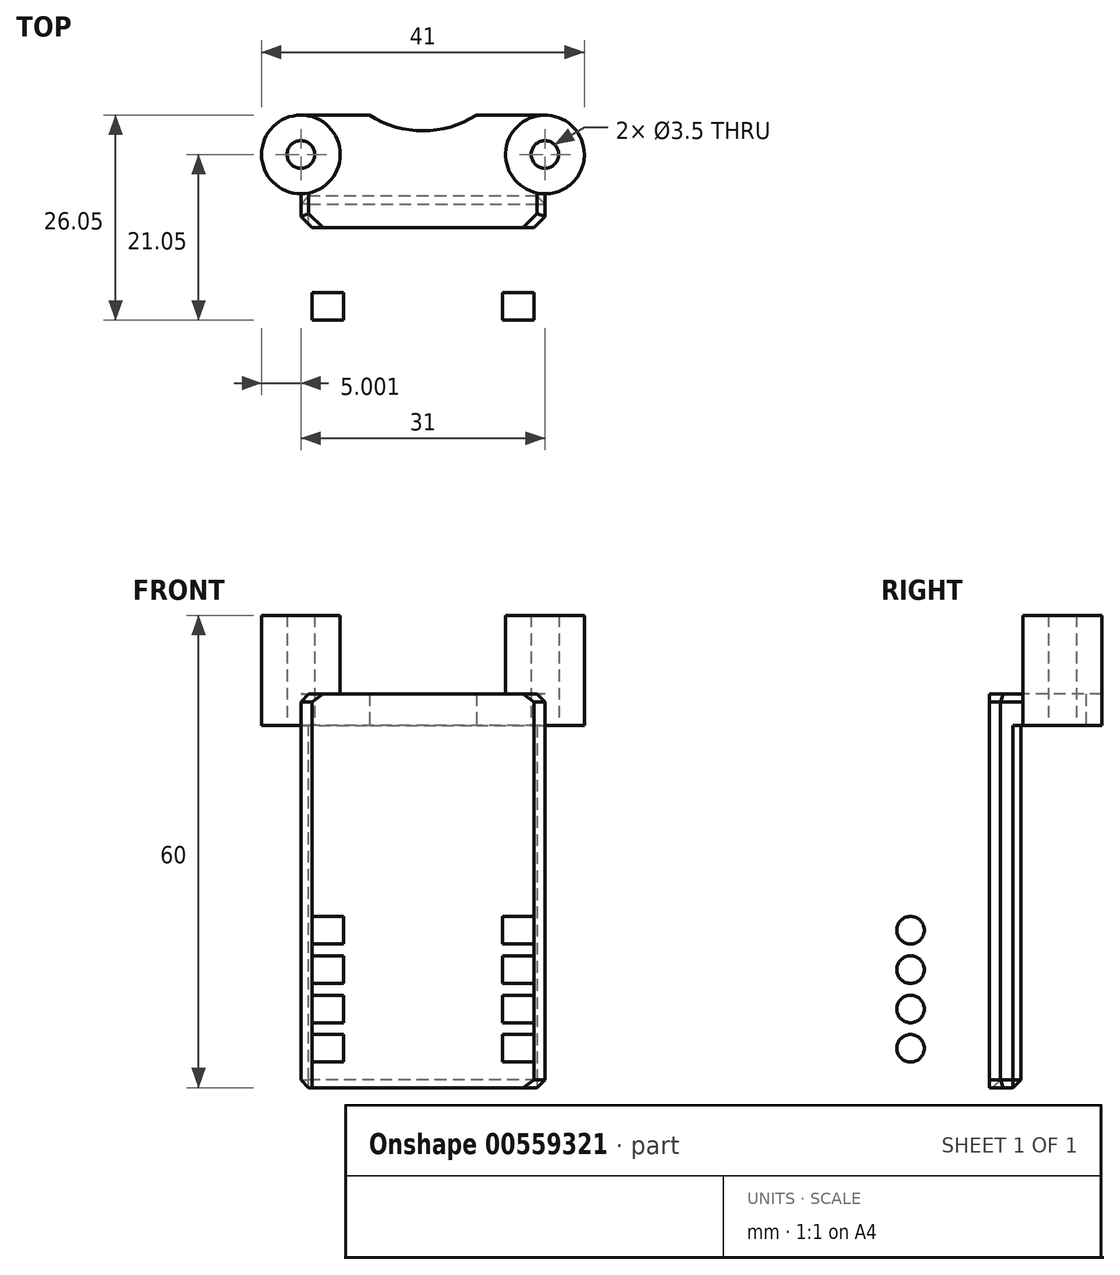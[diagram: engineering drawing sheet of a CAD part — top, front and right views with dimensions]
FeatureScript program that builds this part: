
annotation { "Feature Type Name" : "Feature", "Feature Type Description" : "" }
export const myFeature = defineFeature(function(context is Context, id is Id, definition is map)
    precondition{}
    {
        {
            var Q0;
            Q0=qCreatedBy(makeId("Top.planeOp"),FACE);
            var sketch = newSketch(context, id + "F0", { "sketchPlane" : qUnion([Q0])});
            skLineSegment(sketch, "E0", {"start": v(-4.15, -31) * mm, "end": v(26.85, -31) * mm});
            skCircle(sketch, "E1", {"center": v(26.85, -31) * mm, "radius": 1.75 * mm});
            skCircle(sketch, "E2", {"center": v(-4.15, -31) * mm, "radius": 1.75 * mm});
            skCircle(sketch, "E3", {"center": v(-4.15, -31) * mm, "radius": 5 * mm});
            skCircle(sketch, "E4", {"center": v(26.85, -31) * mm, "radius": 5 * mm});
            skLineSegment(sketch, "E5", {"start": v(-4.15, -31) * mm, "end": v(-4.15, -26) * mm, "construction": true});
            skLineSegment(sketch, "E6", {"start": v(-4.15, -26) * mm, "end": v(26.85, -26) * mm});
            skLineSegment(sketch, "E7", {"start": v(26.85, -26) * mm, "end": v(26.85, -36) * mm, "construction": true});
            skLineSegment(sketch, "E8", {"start": v(26.85, -36) * mm, "end": v(-4.15, -36) * mm});
            skLineSegment(sketch, "E9", {"start": v(-4.15, -36) * mm, "end": v(-4.15, -31) * mm, "construction": true});
            skLineSegment(sketch, "E10", {"start": v(26.85, -31) * mm, "end": v(26.85, 0) * mm});
            skLineSegment(sketch, "E11", {"start": v(26.85, 0) * mm, "end": v(-4.15, 0) * mm});
            skLineSegment(sketch, "E12", {"start": v(-4.15, 0) * mm, "end": v(-4.15, -31) * mm});
            skLineSegment(sketch, "E13", {"start": v(-4.15, -31) * mm, "end": v(26.85, 0) * mm, "construction": true});
            skLineSegment(sketch, "E14", {"start": v(-4.15, 0) * mm, "end": v(26.85, -31) * mm, "construction": true});
            skCircle(sketch, "E15", {"center": v(11.35, -15.5) * mm, "radius": 12.5 * mm});
            skSolve(sketch);
        }
        {
            var Q0;
            Q0=makeQuery(id+"F0.imprint","IMPRINT",FACE,{"disambiguationData":[TD([[makeQuery(id+"F0.imprint","IMPRINT",EDGE,{"derivedFrom":sQuery(id+"F0.wireOp",EDGE,"E2")}),-1.0]])]});
            var Q1;
            {var subQ5=sQuery(id+"F0.wireOp",EDGE,"E6");Q1=makeQuery(id+"F0.imprint","IMPRINT",FACE,{"disambiguationData":[TD([[makeQuery(id+"F0.imprint","IMPRINT",EDGE,{"derivedFrom":subQ5}),-1.0]])]});}
            var Q2;
            Q2=makeQuery(id+"F0.imprint","IMPRINT",FACE,{"disambiguationData":[TD([[makeQuery(id+"F0.imprint","IMPRINT",EDGE,{"derivedFrom":sQuery(id+"F0.wireOp",EDGE,"E1")}),-1.0]])]});
            var Q3;
            {var subQ5=sQuery(id+"F0.wireOp",EDGE,"E8");Q3=makeQuery(id+"F0.imprint","IMPRINT",FACE,{"disambiguationData":[TD([[makeQuery(id+"F0.imprint","IMPRINT",EDGE,{"derivedFrom":subQ5}),-1.0]])]});}
            var Q4;
            {var subQ1=sQuery(id+"F0.wireOp",EDGE,"E4");var subQ4=sQuery(id+"F0.wireOp",EDGE,"E0");var subQ5=makeQuery(id+"F0.imprint","INTERSECT",VERTEX,{"derivedFrom":[subQ4,subQ1]});Q4=makeQuery(id+"F0.imprint","IMPRINT",FACE,{"disambiguationData":[TD([[makeQuery(id+"F0.imprint","IMPRINT",EDGE,{"disambiguationData":[TD([[subQ5,-1.0]])],"derivedFrom":subQ4}),-1.0]])]});}
            var Q5;
            {var subQ4=sQuery(id+"F0.wireOp",EDGE,"E2");var subQ5=sQuery(id+"F0.wireOp",EDGE,"E0");var subQ6=makeQuery(id+"F0.imprint","INTERSECT",VERTEX,{"derivedFrom":[subQ5,subQ4]});Q5=makeQuery(id+"F0.imprint","IMPRINT",FACE,{"disambiguationData":[TD([[makeQuery(id+"F0.imprint","IMPRINT",EDGE,{"disambiguationData":[TD([[subQ6,-1.0]])],"derivedFrom":subQ5}),-1.0]])]});}
            extrude(context, id + "F1", {"entities" : qUnion([Q0, Q1, Q2, Q3, Q4, Q5]), "depth" : 4 * mm, "offsetDistance" : 25 * mm});
        }
        {
            var Q0;
            Q0=makeQuery(id+"F0.imprint","IMPRINT",FACE,{"disambiguationData":[TD([[makeQuery(id+"F0.imprint","IMPRINT",EDGE,{"derivedFrom":sQuery(id+"F0.wireOp",EDGE,"E2")}),-1.0]])]});
            var Q1;
            Q1=makeQuery(id+"F0.imprint","IMPRINT",FACE,{"disambiguationData":[TD([[makeQuery(id+"F0.imprint","IMPRINT",EDGE,{"derivedFrom":sQuery(id+"F0.wireOp",EDGE,"E1")}),-1.0]])]});
            var Q2;
            {var subQ4=sQuery(id+"F0.wireOp",EDGE,"E2");var subQ5=sQuery(id+"F0.wireOp",EDGE,"E0");var subQ6=makeQuery(id+"F0.imprint","INTERSECT",VERTEX,{"derivedFrom":[subQ5,subQ4]});Q2=makeQuery(id+"F0.imprint","IMPRINT",FACE,{"disambiguationData":[TD([[makeQuery(id+"F0.imprint","IMPRINT",EDGE,{"disambiguationData":[TD([[subQ6,-1.0]])],"derivedFrom":subQ5}),-1.0]])]});}
            var Q3;
            {var subQ1=sQuery(id+"F0.wireOp",EDGE,"E4");var subQ4=sQuery(id+"F0.wireOp",EDGE,"E0");var subQ5=makeQuery(id+"F0.imprint","INTERSECT",VERTEX,{"derivedFrom":[subQ4,subQ1]});Q3=makeQuery(id+"F0.imprint","IMPRINT",FACE,{"disambiguationData":[TD([[makeQuery(id+"F0.imprint","IMPRINT",EDGE,{"disambiguationData":[TD([[subQ5,-1.0]])],"derivedFrom":subQ4}),-1.0]])]});}
            extrude(context, id + "F2", {"entities" : qUnion([Q0, Q1, Q2, Q3]), "operationType" : NewBodyOperationType.ADD, "depth" : 14 * mm, "offsetDistance" : 25 * mm});
        }
        {
            var Q0;
            Q0=makeQuery(id+"F1.opExtrude","SWEPT_FACE",FACE,{"disambiguationData":[OSD([sQuery(id+"F0.wireOp",EDGE,"E8")])]});
            extrude(context, id + "F3", {"entities" : qUnion([Q0]), "operationType" : NewBodyOperationType.ADD, "depth" : 4.3 * mm, "offsetDistance" : 25 * mm});
        }
        {
            var Q0;
            {var subQ0=sQuery(id+"F0.wireOp",EDGE,"E8");Q0=makeQuery(id+"F3.boolean.opBoolean","MERGE",FACE,{"derivedFrom":[makeQuery(id+"F1.opExtrude","CAP_FACE",FACE,{"disambiguationData":[OSD([sQuery(id+"F0.wireOp",EDGE,"E1"),sQuery(id+"F0.wireOp",EDGE,"E2"),sQuery(id+"F0.wireOp",EDGE,"E3"),sQuery(id+"F0.wireOp",EDGE,"E4"),sQuery(id+"F0.wireOp",EDGE,"E6"),subQ0,sQuery(id+"F0.wireOp",EDGE,"E15")])],"isStart":true}),makeQuery(id+"F3.opExtrude","SWEPT_FACE",FACE,{"disambiguationData":[OSD([subQ0]),TDD([makeQuery(id+"F1.opExtrude","CAP_EDGE",EDGE,{"disambiguationData":[OSD([subQ0])],"isStart":true})])]})]});}
            var sketch = newSketch(context, id + "F4", { "sketchPlane" : qUnion([Q0])});
            skLineSegment(sketch, "E16.bottom", {"start": v(26.85, 40.3) * mm, "end": v(-4.15, 40.3) * mm});
            skLineSegment(sketch, "E16.top", {"start": v(26.85, 36.3) * mm, "end": v(-4.15, 36.3) * mm});
            skLineSegment(sketch, "E16.left", {"start": v(26.85, 40.3) * mm, "end": v(26.85, 36.3) * mm});
            skLineSegment(sketch, "E16.right", {"start": v(-4.15, 40.3) * mm, "end": v(-4.15, 36.3) * mm});
            skSolve(sketch);
        }
        {
            var Q0;
            Q0=makeQuery(id+"F4.imprint","IMPRINT",FACE,{"disambiguationData":[TD([[makeQuery(id+"F4.imprint","IMPRINT",EDGE,{"derivedFrom":sQuery(id+"F4.wireOp",EDGE,"E16.bottom")}),1.0]])]});
            extrude(context, id + "F5", {"entities" : qUnion([Q0]), "operationType" : NewBodyOperationType.ADD, "depth" : 46 * mm, "offsetDistance" : 25 * mm});
        }
        {
            var Q0;
            Q0=makeQuery(id+"F5.boolean.opBoolean","MERGE",FACE,{"derivedFrom":[makeQuery(id+"F3.opExtrude","CAP_FACE",FACE,{"disambiguationData":[OSD([sQuery(id+"F0.wireOp",EDGE,"E8")])],"isStart":false}),makeQuery(id+"F5.opExtrude","SWEPT_FACE",FACE,{"disambiguationData":[OSD([sQuery(id+"F4.wireOp",EDGE,"E16.bottom")])]})]});
            var sketch = newSketch(context, id + "F6", { "sketchPlane" : qUnion([Q0])});
            skLineSegment(sketch, "E17", {"start": v(11.35, 4) * mm, "end": v(11.35, -46) * mm, "construction": true});
            skLineSegment(sketch, "E18", {"start": v(21.45, -21) * mm, "end": v(1.25, -21) * mm, "construction": true});
            skPoint(sketch, "E18.startSnap0", {"position": v(11.35, -21) * mm});
            skLineSegment(sketch, "E19", {"start": v(21.45, -46) * mm, "end": v(21.45, 4) * mm});
            skLineSegment(sketch, "E20", {"start": v(1.25, 4) * mm, "end": v(1.25, -46) * mm});
            skLineSegment(sketch, "E21", {"start": v(21.45, -21) * mm, "end": v(25.45, -21) * mm, "construction": true});
            skLineSegment(sketch, "E22", {"start": v(1.25, -21) * mm, "end": v(-2.75, -21) * mm, "construction": true});
            skLineSegment(sketch, "E23", {"start": v(25.45, -46) * mm, "end": v(25.45, 4) * mm});
            skLineSegment(sketch, "E24", {"start": v(-2.75, 4) * mm, "end": v(-2.75, -46) * mm});
            skSolve(sketch);
        }
        {
            var Q0;
            {var subQ0=sQuery(id+"F6.wireOp",EDGE,"E19");Q0=makeQuery(id+"F6.imprint","IMPRINT",FACE,{"disambiguationData":[TD([[makeQuery(id+"F6.imprint","IMPRINT",EDGE,{"derivedFrom":subQ0}),-1.0]])]});}
            var Q1;
            {var subQ0=sQuery(id+"F6.wireOp",EDGE,"E20");Q1=makeQuery(id+"F6.imprint","IMPRINT",FACE,{"disambiguationData":[TD([[makeQuery(id+"F6.imprint","IMPRINT",EDGE,{"derivedFrom":subQ0}),-1.0]])]});}
            extrude(context, id + "F7", {"entities" : qUnion([Q0, Q1]), "operationType" : NewBodyOperationType.ADD, "depth" : 20 * mm, "offsetDistance" : 25 * mm});
        }
        {
            var Q0;
            Q0=makeQuery(id+"F7.opExtrude","SWEPT_FACE",FACE,{"disambiguationData":[OSD([sQuery(id+"F6.wireOp",EDGE,"E24")])]});
            var sketch = newSketch(context, id + "F8", { "sketchPlane" : qUnion([Q0])});
            skLineSegment(sketch, "E25", {"start": v(60.3, -21) * mm, "end": v(40.3, -21) * mm, "construction": true});
            skLineSegment(sketch, "E26", {"start": v(50.3, -21) * mm, "end": v(50.3, -16) * mm, "construction": true});
            skLineSegment(sketch, "E27", {"start": v(50.3, -16) * mm, "end": v(50.3, -11) * mm, "construction": true});
            skLineSegment(sketch, "E28", {"start": v(50.3, -11) * mm, "end": v(50.3, -6) * mm, "construction": true});
            skLineSegment(sketch, "E29", {"start": v(50.3, -6) * mm, "end": v(50.3, -1) * mm, "construction": true});
            skCircle(sketch, "E30", {"center": v(50.3, -6) * mm, "radius": 1.75 * mm});
            skCircle(sketch, "E31", {"center": v(50.3, -1) * mm, "radius": 1.75 * mm});
            skCircle(sketch, "E32", {"center": v(50.3, -11) * mm, "radius": 1.75 * mm});
            skCircle(sketch, "E33", {"center": v(50.3, -16) * mm, "radius": 1.75 * mm});
            skLineSegment(sketch, "E34.MirrorCS", {"start": v(50.3, -21) * mm, "end": v(50.3, -26) * mm, "construction": true});
            skCircle(sketch, "E35.MirrorC", {"center": v(50.3, -41) * mm, "radius": 1.75 * mm});
            skCircle(sketch, "E36.MirrorC", {"center": v(50.3, -31) * mm, "radius": 1.75 * mm});
            skLineSegment(sketch, "E37.MirrorCS", {"start": v(50.3, -26) * mm, "end": v(50.3, -31) * mm, "construction": true});
            skLineSegment(sketch, "E38.MirrorCS", {"start": v(50.3, -31) * mm, "end": v(50.3, -36) * mm, "construction": true});
            skLineSegment(sketch, "E39.MirrorCS", {"start": v(50.3, -36) * mm, "end": v(50.3, -41) * mm, "construction": true});
            skCircle(sketch, "E40.MirrorC", {"center": v(50.3, -36) * mm, "radius": 1.75 * mm});
            skCircle(sketch, "E41.MirrorC", {"center": v(50.3, -26) * mm, "radius": 1.75 * mm});
            skSolve(sketch);
        }
        {
            var Q0;
            Q0=makeQuery(id+"F8.imprint","IMPRINT",FACE,{"disambiguationData":[TD([[makeQuery(id+"F8.imprint","IMPRINT",EDGE,{"derivedFrom":sQuery(id+"F8.wireOp",EDGE,"E31")}),1.0]])]});
            var Q1;
            Q1=makeQuery(id+"F8.imprint","IMPRINT",FACE,{"disambiguationData":[TD([[makeQuery(id+"F8.imprint","IMPRINT",EDGE,{"derivedFrom":sQuery(id+"F8.wireOp",EDGE,"E30")}),1.0]])]});
            var Q2;
            Q2=makeQuery(id+"F8.imprint","IMPRINT",FACE,{"disambiguationData":[TD([[makeQuery(id+"F8.imprint","IMPRINT",EDGE,{"derivedFrom":sQuery(id+"F8.wireOp",EDGE,"E33")}),1.0]])]});
            var Q3;
            Q3=makeQuery(id+"F8.imprint","IMPRINT",FACE,{"disambiguationData":[TD([[makeQuery(id+"F8.imprint","IMPRINT",EDGE,{"derivedFrom":sQuery(id+"F8.wireOp",EDGE,"E41.MirrorC")}),-1.0]])]});
            var Q4;
            Q4=makeQuery(id+"F8.imprint","IMPRINT",FACE,{"disambiguationData":[TD([[makeQuery(id+"F8.imprint","IMPRINT",EDGE,{"derivedFrom":sQuery(id+"F8.wireOp",EDGE,"E36.MirrorC")}),-1.0]])]});
            var Q5;
            Q5=makeQuery(id+"F8.imprint","IMPRINT",FACE,{"disambiguationData":[TD([[makeQuery(id+"F8.imprint","IMPRINT",EDGE,{"derivedFrom":sQuery(id+"F8.wireOp",EDGE,"E40.MirrorC")}),-1.0]])]});
            var Q6;
            Q6=makeQuery(id+"F8.imprint","IMPRINT",FACE,{"disambiguationData":[TD([[makeQuery(id+"F8.imprint","IMPRINT",EDGE,{"derivedFrom":sQuery(id+"F8.wireOp",EDGE,"E35.MirrorC")}),-1.0]])]});
            var Q7;
            Q7=makeQuery(id+"F8.imprint","IMPRINT",FACE,{"disambiguationData":[TD([[makeQuery(id+"F8.imprint","IMPRINT",EDGE,{"derivedFrom":sQuery(id+"F8.wireOp",EDGE,"E32")}),1.0]])]});
            extrude(context, id + "F9", {"entities" : qUnion([Q0, Q1, Q2, Q3, Q4, Q5, Q6, Q7]), "operationType" : NewBodyOperationType.REMOVE, "endBound" : BoundingType.THROUGH_ALL, "oppositeDirection" : true, "depth" : 25 * mm, "offsetDistance" : 25 * mm});
        }
        {
            var Q0;
            Q0=makeQuery(id+"F5.boolean.opBoolean","MERGE",EDGE,{"derivedFrom":[makeQuery(id+"F3.opExtrude","CAP_EDGE",EDGE,{"disambiguationData":[OSD([sQuery(id+"F0.wireOp",EDGE,"E4"),sQuery(id+"F0.wireOp",EDGE,"E8")])],"isStart":false}),makeQuery(id+"F5.opExtrude","SWEPT_EDGE",EDGE,{"disambiguationData":[OSD([sQuery(id+"F4.wireOp",EDGE,"E16.bottom"),sQuery(id+"F4.wireOp",EDGE,"E16.left")])]})]});
            var Q1;
            Q1=makeQuery(id+"F5.boolean.opBoolean","MERGE",EDGE,{"derivedFrom":[makeQuery(id+"F3.opExtrude","CAP_EDGE",EDGE,{"disambiguationData":[OSD([sQuery(id+"F0.wireOp",EDGE,"E3"),sQuery(id+"F0.wireOp",EDGE,"E8")])],"isStart":false}),makeQuery(id+"F5.opExtrude","SWEPT_EDGE",EDGE,{"disambiguationData":[OSD([sQuery(id+"F4.wireOp",EDGE,"E16.bottom"),sQuery(id+"F4.wireOp",EDGE,"E16.right")])]})]});
            chamfer(context, id + "F10", {"entities" : qUnion([Q0, Q1]), "width" : 1.4 * mm, "tangentPropagation" : true});
        }
        {
            var Q0;
            Q0=makeQuery(id+"F7.opExtrude","CAP_EDGE",EDGE,{"disambiguationData":[OSD([sQuery(id+"F6.wireOp",EDGE,"E24")])],"isStart":false});
            var Q1;
            Q1=makeQuery(id+"F7.opExtrude","CAP_EDGE",EDGE,{"disambiguationData":[OSD([sQuery(id+"F6.wireOp",EDGE,"E20")])],"isStart":false});
            var Q2;
            Q2=makeQuery(id+"F7.opExtrude","CAP_EDGE",EDGE,{"disambiguationData":[OSD([sQuery(id+"F6.wireOp",EDGE,"E19")])],"isStart":false});
            var Q3;
            Q3=makeQuery(id+"F7.opExtrude","CAP_EDGE",EDGE,{"disambiguationData":[OSD([sQuery(id+"F6.wireOp",EDGE,"E23")])],"isStart":false});
            var Q4;
            {var subQ0=sQuery(id+"F0.wireOp",EDGE,"E8");var subQ1=makeQuery(id+"F3.opExtrude","CAP_EDGE",EDGE,{"disambiguationData":[OSD([subQ0]),TDD([makeQuery(id+"F1.opExtrude","CAP_EDGE",EDGE,{"disambiguationData":[OSD([subQ0])],"isStart":false})])],"isStart":false});Q4=makeQuery(id+"F7.opExtrude","CAP_EDGE",EDGE,{"disambiguationData":[OSD([subQ0]),TDD([makeQuery(id+"F6.imprint","IMPRINT",EDGE,{"disambiguationData":[TD([[makeQuery(id+"F6.imprint","INTERSECT",VERTEX,{"derivedFrom":[subQ1,sQuery(id+"F6.wireOp",EDGE,"E19")]}),1.0]])],"derivedFrom":subQ1})])],"isStart":false});}
            var Q5;
            {var subQ0=sQuery(id+"F4.wireOp",EDGE,"E16.bottom");var subQ1=makeQuery(id+"F5.opExtrude","CAP_EDGE",EDGE,{"disambiguationData":[OSD([subQ0])],"isStart":false});Q5=makeQuery(id+"F7.opExtrude","CAP_EDGE",EDGE,{"disambiguationData":[OSD([subQ0]),TDD([makeQuery(id+"F6.imprint","IMPRINT",EDGE,{"disambiguationData":[TD([[makeQuery(id+"F6.imprint","INTERSECT",VERTEX,{"derivedFrom":[subQ1,sQuery(id+"F6.wireOp",EDGE,"E19")]}),1.0]])],"derivedFrom":subQ1})])],"isStart":false});}
            var Q6;
            {var subQ0=sQuery(id+"F4.wireOp",EDGE,"E16.bottom");var subQ1=makeQuery(id+"F5.opExtrude","CAP_EDGE",EDGE,{"disambiguationData":[OSD([subQ0])],"isStart":false});Q6=makeQuery(id+"F7.opExtrude","CAP_EDGE",EDGE,{"disambiguationData":[OSD([subQ0]),TDD([makeQuery(id+"F6.imprint","IMPRINT",EDGE,{"disambiguationData":[TD([[makeQuery(id+"F6.imprint","INTERSECT",VERTEX,{"derivedFrom":[subQ1,sQuery(id+"F6.wireOp",EDGE,"E20")]}),-1.0]])],"derivedFrom":subQ1})])],"isStart":false});}
            var Q7;
            {var subQ0=sQuery(id+"F0.wireOp",EDGE,"E8");var subQ1=makeQuery(id+"F3.opExtrude","CAP_EDGE",EDGE,{"disambiguationData":[OSD([subQ0]),TDD([makeQuery(id+"F1.opExtrude","CAP_EDGE",EDGE,{"disambiguationData":[OSD([subQ0])],"isStart":false})])],"isStart":false});Q7=makeQuery(id+"F7.opExtrude","CAP_EDGE",EDGE,{"disambiguationData":[OSD([subQ0]),TDD([makeQuery(id+"F6.imprint","IMPRINT",EDGE,{"disambiguationData":[TD([[makeQuery(id+"F6.imprint","INTERSECT",VERTEX,{"derivedFrom":[subQ1,sQuery(id+"F6.wireOp",EDGE,"E20")]}),-1.0]])],"derivedFrom":subQ1})])],"isStart":false});}
            var Q8;
            Q8=makeQuery(id+"F7.opExtrude","SWEPT_EDGE",EDGE,{"disambiguationData":[OSD([sQuery(id+"F0.wireOp",EDGE,"E8"),sQuery(id+"F6.wireOp",EDGE,"E20")])]});
            var Q9;
            Q9=makeQuery(id+"F7.opExtrude","SWEPT_EDGE",EDGE,{"disambiguationData":[OSD([sQuery(id+"F0.wireOp",EDGE,"E8"),sQuery(id+"F6.wireOp",EDGE,"E24")])]});
            var Q10;
            Q10=makeQuery(id+"F7.opExtrude","SWEPT_EDGE",EDGE,{"disambiguationData":[OSD([sQuery(id+"F0.wireOp",EDGE,"E8"),sQuery(id+"F6.wireOp",EDGE,"E19")])]});
            var Q11;
            Q11=makeQuery(id+"F7.opExtrude","SWEPT_EDGE",EDGE,{"disambiguationData":[OSD([sQuery(id+"F0.wireOp",EDGE,"E8"),sQuery(id+"F6.wireOp",EDGE,"E23")])]});
            var Q12;
            Q12=makeQuery(id+"F7.opExtrude","SWEPT_EDGE",EDGE,{"disambiguationData":[OSD([sQuery(id+"F4.wireOp",EDGE,"E16.bottom"),sQuery(id+"F6.wireOp",EDGE,"E24")])]});
            var Q13;
            Q13=makeQuery(id+"F7.opExtrude","SWEPT_EDGE",EDGE,{"disambiguationData":[OSD([sQuery(id+"F4.wireOp",EDGE,"E16.bottom"),sQuery(id+"F6.wireOp",EDGE,"E20")])]});
            var Q14;
            Q14=makeQuery(id+"F7.opExtrude","SWEPT_EDGE",EDGE,{"disambiguationData":[OSD([sQuery(id+"F4.wireOp",EDGE,"E16.bottom"),sQuery(id+"F6.wireOp",EDGE,"E23")])]});
            var Q15;
            Q15=makeQuery(id+"F7.opExtrude","SWEPT_EDGE",EDGE,{"disambiguationData":[OSD([sQuery(id+"F4.wireOp",EDGE,"E16.bottom"),sQuery(id+"F6.wireOp",EDGE,"E19")])]});
            var Q16;
            Q16=makeQuery(id+"F5.opExtrude","SWEPT_EDGE",EDGE,{"disambiguationData":[OSD([sQuery(id+"F0.wireOp",EDGE,"E3"),sQuery(id+"F0.wireOp",EDGE,"E8"),sQuery(id+"F4.wireOp",EDGE,"E16.top"),sQuery(id+"F4.wireOp",EDGE,"E16.right")])]});
            var Q17;
            {var subQ0=sQuery(id+"F6.wireOp",EDGE,"E19");var subQ2=sQuery(id+"F4.wireOp",EDGE,"E16.bottom");var subQ3=makeQuery(id+"F5.opExtrude","CAP_EDGE",EDGE,{"disambiguationData":[OSD([subQ2])],"isStart":false});Q17=makeQuery(id+"F7.boolean.opBoolean","SPLIT",EDGE,{"disambiguationData":[TD([makeQuery(id+"F7.opExtrude","SWEPT_FACE",FACE,{"disambiguationData":[OSD([subQ0])]})])],"derivedFrom":subQ3});}
            var Q18;
            Q18=makeQuery(id+"F5.opExtrude","CAP_EDGE",EDGE,{"disambiguationData":[OSD([sQuery(id+"F4.wireOp",EDGE,"E16.top")])],"isStart":false});
            var Q19;
            Q19=makeQuery(id+"F5.opExtrude","CAP_EDGE",EDGE,{"disambiguationData":[OSD([sQuery(id+"F4.wireOp",EDGE,"E16.right")])],"isStart":false});
            var Q20;
            Q20=makeQuery(id+"F5.opExtrude","CAP_EDGE",EDGE,{"disambiguationData":[OSD([sQuery(id+"F4.wireOp",EDGE,"E16.left")])],"isStart":false});
            var Q21;
            {var subQ0=sQuery(id+"F4.wireOp",EDGE,"E16.bottom");var subQ1=makeQuery(id+"F5.opExtrude","CAP_EDGE",EDGE,{"disambiguationData":[OSD([subQ0])],"isStart":false});var subQ2=sQuery(id+"F4.wireOp",EDGE,"E16.left");Q21=makeQuery(id+"F10.opChamfer","BLEND_EDGE",EDGE,{"blendedFrom":[makeQuery(id+"F5.boolean.opBoolean","MERGE",EDGE,{"derivedFrom":[makeQuery(id+"F3.opExtrude","CAP_EDGE",EDGE,{"disambiguationData":[OSD([sQuery(id+"F0.wireOp",EDGE,"E4"),sQuery(id+"F0.wireOp",EDGE,"E8")])],"isStart":false}),makeQuery(id+"F5.opExtrude","SWEPT_EDGE",EDGE,{"disambiguationData":[OSD([subQ0,subQ2])]})]}),makeQuery(id+"F7.boolean.opBoolean","MERGE",FACE,{"derivedFrom":[makeQuery(id+"F5.opExtrude","CAP_FACE",FACE,{"disambiguationData":[OSD([subQ0,sQuery(id+"F4.wireOp",EDGE,"E16.top"),subQ2,sQuery(id+"F4.wireOp",EDGE,"E16.right")])],"isStart":false}),makeQuery(id+"F7.opExtrude","SWEPT_FACE",FACE,{"disambiguationData":[OSD([subQ0]),TDD([makeQuery(id+"F6.imprint","IMPRINT",EDGE,{"disambiguationData":[TD([[makeQuery(id+"F6.imprint","INTERSECT",VERTEX,{"derivedFrom":[subQ1,sQuery(id+"F6.wireOp",EDGE,"E19")]}),1.0]])],"derivedFrom":subQ1})])]}),makeQuery(id+"F7.opExtrude","SWEPT_FACE",FACE,{"disambiguationData":[OSD([subQ0]),TDD([makeQuery(id+"F6.imprint","IMPRINT",EDGE,{"disambiguationData":[TD([[makeQuery(id+"F6.imprint","INTERSECT",VERTEX,{"derivedFrom":[subQ1,sQuery(id+"F6.wireOp",EDGE,"E20")]}),-1.0]])],"derivedFrom":subQ1})])]})]})],"blendedInto":[makeQuery(id+"F7.boolean.opBoolean","MERGE",FACE,{"derivedFrom":[makeQuery(id+"F5.opExtrude","CAP_FACE",FACE,{"disambiguationData":[OSD([subQ0,sQuery(id+"F4.wireOp",EDGE,"E16.top"),subQ2,sQuery(id+"F4.wireOp",EDGE,"E16.right")])],"isStart":false}),makeQuery(id+"F7.opExtrude","SWEPT_FACE",FACE,{"disambiguationData":[OSD([subQ0]),TDD([makeQuery(id+"F6.imprint","IMPRINT",EDGE,{"disambiguationData":[TD([[makeQuery(id+"F6.imprint","INTERSECT",VERTEX,{"derivedFrom":[subQ1,sQuery(id+"F6.wireOp",EDGE,"E19")]}),1.0]])],"derivedFrom":subQ1})])]}),makeQuery(id+"F7.opExtrude","SWEPT_FACE",FACE,{"disambiguationData":[OSD([subQ0]),TDD([makeQuery(id+"F6.imprint","IMPRINT",EDGE,{"disambiguationData":[TD([[makeQuery(id+"F6.imprint","INTERSECT",VERTEX,{"derivedFrom":[subQ1,sQuery(id+"F6.wireOp",EDGE,"E20")]}),-1.0]])],"derivedFrom":subQ1})])]})]})]});}
            var Q22;
            Q22=makeQuery(id+"F5.opExtrude","SWEPT_EDGE",EDGE,{"disambiguationData":[OSD([sQuery(id+"F0.wireOp",EDGE,"E4"),sQuery(id+"F0.wireOp",EDGE,"E8"),sQuery(id+"F4.wireOp",EDGE,"E16.top"),sQuery(id+"F4.wireOp",EDGE,"E16.left")])]});
            var Q23;
            {var subQ0=sQuery(id+"F0.wireOp",EDGE,"E8");var subQ1=makeQuery(id+"F1.opExtrude","CAP_EDGE",EDGE,{"disambiguationData":[OSD([subQ0])],"isStart":false});var subQ2=sQuery(id+"F6.wireOp",EDGE,"E19");var subQ4=makeQuery(id+"F3.opExtrude","CAP_EDGE",EDGE,{"disambiguationData":[OSD([subQ0]),TDD([subQ1])],"isStart":false});Q23=makeQuery(id+"F7.boolean.opBoolean","SPLIT",EDGE,{"disambiguationData":[TD([makeQuery(id+"F7.opExtrude","SWEPT_FACE",FACE,{"disambiguationData":[OSD([subQ2])]})])],"derivedFrom":subQ4});}
            var Q24;
            {var subQ0=sQuery(id+"F0.wireOp",EDGE,"E8");var subQ1=sQuery(id+"F0.wireOp",EDGE,"E4");Q24=makeQuery(id+"F3.opExtrude","SWEPT_EDGE",EDGE,{"disambiguationData":[OSD([subQ1,subQ0]),TDD([makeQuery(id+"F1.opExtrude","CAP_VERTEX",VERTEX,{"disambiguationData":[OSD([subQ1,subQ0])],"isStart":false})])]});}
            var Q25;
            {var subQ0=sQuery(id+"F0.wireOp",EDGE,"E8");var subQ1=makeQuery(id+"F1.opExtrude","CAP_EDGE",EDGE,{"disambiguationData":[OSD([subQ0])],"isStart":false});var subQ2=makeQuery(id+"F3.opExtrude","CAP_EDGE",EDGE,{"disambiguationData":[OSD([subQ0]),TDD([subQ1])],"isStart":false});var subQ3=sQuery(id+"F0.wireOp",EDGE,"E4");Q25=makeQuery(id+"F10.opChamfer","BLEND_EDGE",EDGE,{"blendedFrom":[makeQuery(id+"F5.boolean.opBoolean","MERGE",EDGE,{"derivedFrom":[makeQuery(id+"F3.opExtrude","CAP_EDGE",EDGE,{"disambiguationData":[OSD([subQ3,subQ0])],"isStart":false}),makeQuery(id+"F5.opExtrude","SWEPT_EDGE",EDGE,{"disambiguationData":[OSD([sQuery(id+"F4.wireOp",EDGE,"E16.bottom"),sQuery(id+"F4.wireOp",EDGE,"E16.left")])]})]}),makeQuery(id+"F7.boolean.opBoolean","MERGE",FACE,{"derivedFrom":[makeQuery(id+"F3.boolean.opBoolean","MERGE",FACE,{"derivedFrom":[makeQuery(id+"F1.opExtrude","CAP_FACE",FACE,{"disambiguationData":[OSD([sQuery(id+"F0.wireOp",EDGE,"E1"),sQuery(id+"F0.wireOp",EDGE,"E2"),sQuery(id+"F0.wireOp",EDGE,"E3"),subQ3,sQuery(id+"F0.wireOp",EDGE,"E6"),subQ0,sQuery(id+"F0.wireOp",EDGE,"E15")])],"isStart":false}),makeQuery(id+"F3.opExtrude","SWEPT_FACE",FACE,{"disambiguationData":[OSD([subQ0]),TDD([subQ1])]})]}),makeQuery(id+"F7.opExtrude","SWEPT_FACE",FACE,{"disambiguationData":[OSD([subQ0]),TDD([makeQuery(id+"F6.imprint","IMPRINT",EDGE,{"disambiguationData":[TD([[makeQuery(id+"F6.imprint","INTERSECT",VERTEX,{"derivedFrom":[subQ2,sQuery(id+"F6.wireOp",EDGE,"E19")]}),1.0]])],"derivedFrom":subQ2})])]}),makeQuery(id+"F7.opExtrude","SWEPT_FACE",FACE,{"disambiguationData":[OSD([subQ0]),TDD([makeQuery(id+"F6.imprint","IMPRINT",EDGE,{"disambiguationData":[TD([[makeQuery(id+"F6.imprint","INTERSECT",VERTEX,{"derivedFrom":[subQ2,sQuery(id+"F6.wireOp",EDGE,"E20")]}),-1.0]])],"derivedFrom":subQ2})])]})]})],"blendedInto":[makeQuery(id+"F7.boolean.opBoolean","MERGE",FACE,{"derivedFrom":[makeQuery(id+"F3.boolean.opBoolean","MERGE",FACE,{"derivedFrom":[makeQuery(id+"F1.opExtrude","CAP_FACE",FACE,{"disambiguationData":[OSD([sQuery(id+"F0.wireOp",EDGE,"E1"),sQuery(id+"F0.wireOp",EDGE,"E2"),sQuery(id+"F0.wireOp",EDGE,"E3"),subQ3,sQuery(id+"F0.wireOp",EDGE,"E6"),subQ0,sQuery(id+"F0.wireOp",EDGE,"E15")])],"isStart":false}),makeQuery(id+"F3.opExtrude","SWEPT_FACE",FACE,{"disambiguationData":[OSD([subQ0]),TDD([subQ1])]})]}),makeQuery(id+"F7.opExtrude","SWEPT_FACE",FACE,{"disambiguationData":[OSD([subQ0]),TDD([makeQuery(id+"F6.imprint","IMPRINT",EDGE,{"disambiguationData":[TD([[makeQuery(id+"F6.imprint","INTERSECT",VERTEX,{"derivedFrom":[subQ2,sQuery(id+"F6.wireOp",EDGE,"E19")]}),1.0]])],"derivedFrom":subQ2})])]}),makeQuery(id+"F7.opExtrude","SWEPT_FACE",FACE,{"disambiguationData":[OSD([subQ0]),TDD([makeQuery(id+"F6.imprint","IMPRINT",EDGE,{"disambiguationData":[TD([[makeQuery(id+"F6.imprint","INTERSECT",VERTEX,{"derivedFrom":[subQ2,sQuery(id+"F6.wireOp",EDGE,"E20")]}),-1.0]])],"derivedFrom":subQ2})])]})]})]});}
            var Q26;
            {var subQ0=sQuery(id+"F0.wireOp",EDGE,"E8");var subQ1=sQuery(id+"F0.wireOp",EDGE,"E3");Q26=makeQuery(id+"F3.opExtrude","SWEPT_EDGE",EDGE,{"disambiguationData":[OSD([subQ1,subQ0]),TDD([makeQuery(id+"F1.opExtrude","CAP_VERTEX",VERTEX,{"disambiguationData":[OSD([subQ1,subQ0])],"isStart":false})])]});}
            var Q27;
            {var subQ0=sQuery(id+"F0.wireOp",EDGE,"E8");var subQ1=makeQuery(id+"F1.opExtrude","CAP_EDGE",EDGE,{"disambiguationData":[OSD([subQ0])],"isStart":false});var subQ2=makeQuery(id+"F3.opExtrude","CAP_EDGE",EDGE,{"disambiguationData":[OSD([subQ0]),TDD([subQ1])],"isStart":false});var subQ3=sQuery(id+"F0.wireOp",EDGE,"E3");Q27=makeQuery(id+"F10.opChamfer","BLEND_EDGE",EDGE,{"blendedFrom":[makeQuery(id+"F5.boolean.opBoolean","MERGE",EDGE,{"derivedFrom":[makeQuery(id+"F3.opExtrude","CAP_EDGE",EDGE,{"disambiguationData":[OSD([subQ3,subQ0])],"isStart":false}),makeQuery(id+"F5.opExtrude","SWEPT_EDGE",EDGE,{"disambiguationData":[OSD([sQuery(id+"F4.wireOp",EDGE,"E16.bottom"),sQuery(id+"F4.wireOp",EDGE,"E16.right")])]})]}),makeQuery(id+"F7.boolean.opBoolean","MERGE",FACE,{"derivedFrom":[makeQuery(id+"F3.boolean.opBoolean","MERGE",FACE,{"derivedFrom":[makeQuery(id+"F1.opExtrude","CAP_FACE",FACE,{"disambiguationData":[OSD([sQuery(id+"F0.wireOp",EDGE,"E1"),sQuery(id+"F0.wireOp",EDGE,"E2"),subQ3,sQuery(id+"F0.wireOp",EDGE,"E4"),sQuery(id+"F0.wireOp",EDGE,"E6"),subQ0,sQuery(id+"F0.wireOp",EDGE,"E15")])],"isStart":false}),makeQuery(id+"F3.opExtrude","SWEPT_FACE",FACE,{"disambiguationData":[OSD([subQ0]),TDD([subQ1])]})]}),makeQuery(id+"F7.opExtrude","SWEPT_FACE",FACE,{"disambiguationData":[OSD([subQ0]),TDD([makeQuery(id+"F6.imprint","IMPRINT",EDGE,{"disambiguationData":[TD([[makeQuery(id+"F6.imprint","INTERSECT",VERTEX,{"derivedFrom":[subQ2,sQuery(id+"F6.wireOp",EDGE,"E19")]}),1.0]])],"derivedFrom":subQ2})])]}),makeQuery(id+"F7.opExtrude","SWEPT_FACE",FACE,{"disambiguationData":[OSD([subQ0]),TDD([makeQuery(id+"F6.imprint","IMPRINT",EDGE,{"disambiguationData":[TD([[makeQuery(id+"F6.imprint","INTERSECT",VERTEX,{"derivedFrom":[subQ2,sQuery(id+"F6.wireOp",EDGE,"E20")]}),-1.0]])],"derivedFrom":subQ2})])]})]})],"blendedInto":[makeQuery(id+"F7.boolean.opBoolean","MERGE",FACE,{"derivedFrom":[makeQuery(id+"F3.boolean.opBoolean","MERGE",FACE,{"derivedFrom":[makeQuery(id+"F1.opExtrude","CAP_FACE",FACE,{"disambiguationData":[OSD([sQuery(id+"F0.wireOp",EDGE,"E1"),sQuery(id+"F0.wireOp",EDGE,"E2"),subQ3,sQuery(id+"F0.wireOp",EDGE,"E4"),sQuery(id+"F0.wireOp",EDGE,"E6"),subQ0,sQuery(id+"F0.wireOp",EDGE,"E15")])],"isStart":false}),makeQuery(id+"F3.opExtrude","SWEPT_FACE",FACE,{"disambiguationData":[OSD([subQ0]),TDD([subQ1])]})]}),makeQuery(id+"F7.opExtrude","SWEPT_FACE",FACE,{"disambiguationData":[OSD([subQ0]),TDD([makeQuery(id+"F6.imprint","IMPRINT",EDGE,{"disambiguationData":[TD([[makeQuery(id+"F6.imprint","INTERSECT",VERTEX,{"derivedFrom":[subQ2,sQuery(id+"F6.wireOp",EDGE,"E19")]}),1.0]])],"derivedFrom":subQ2})])]}),makeQuery(id+"F7.opExtrude","SWEPT_FACE",FACE,{"disambiguationData":[OSD([subQ0]),TDD([makeQuery(id+"F6.imprint","IMPRINT",EDGE,{"disambiguationData":[TD([[makeQuery(id+"F6.imprint","INTERSECT",VERTEX,{"derivedFrom":[subQ2,sQuery(id+"F6.wireOp",EDGE,"E20")]}),-1.0]])],"derivedFrom":subQ2})])]})]})]});}
            chamfer(context, id + "F11", {"entities" : qUnion([Q0, Q1, Q2, Q3, Q4, Q5, Q6, Q7, Q8, Q9, Q10, Q11, Q12, Q13, Q14, Q15, Q16, Q17, Q18, Q19, Q20, Q21, Q22, Q23, Q24, Q25, Q26, Q27]), "width" : 1 * mm, "tangentPropagation" : true});
        }
    });
